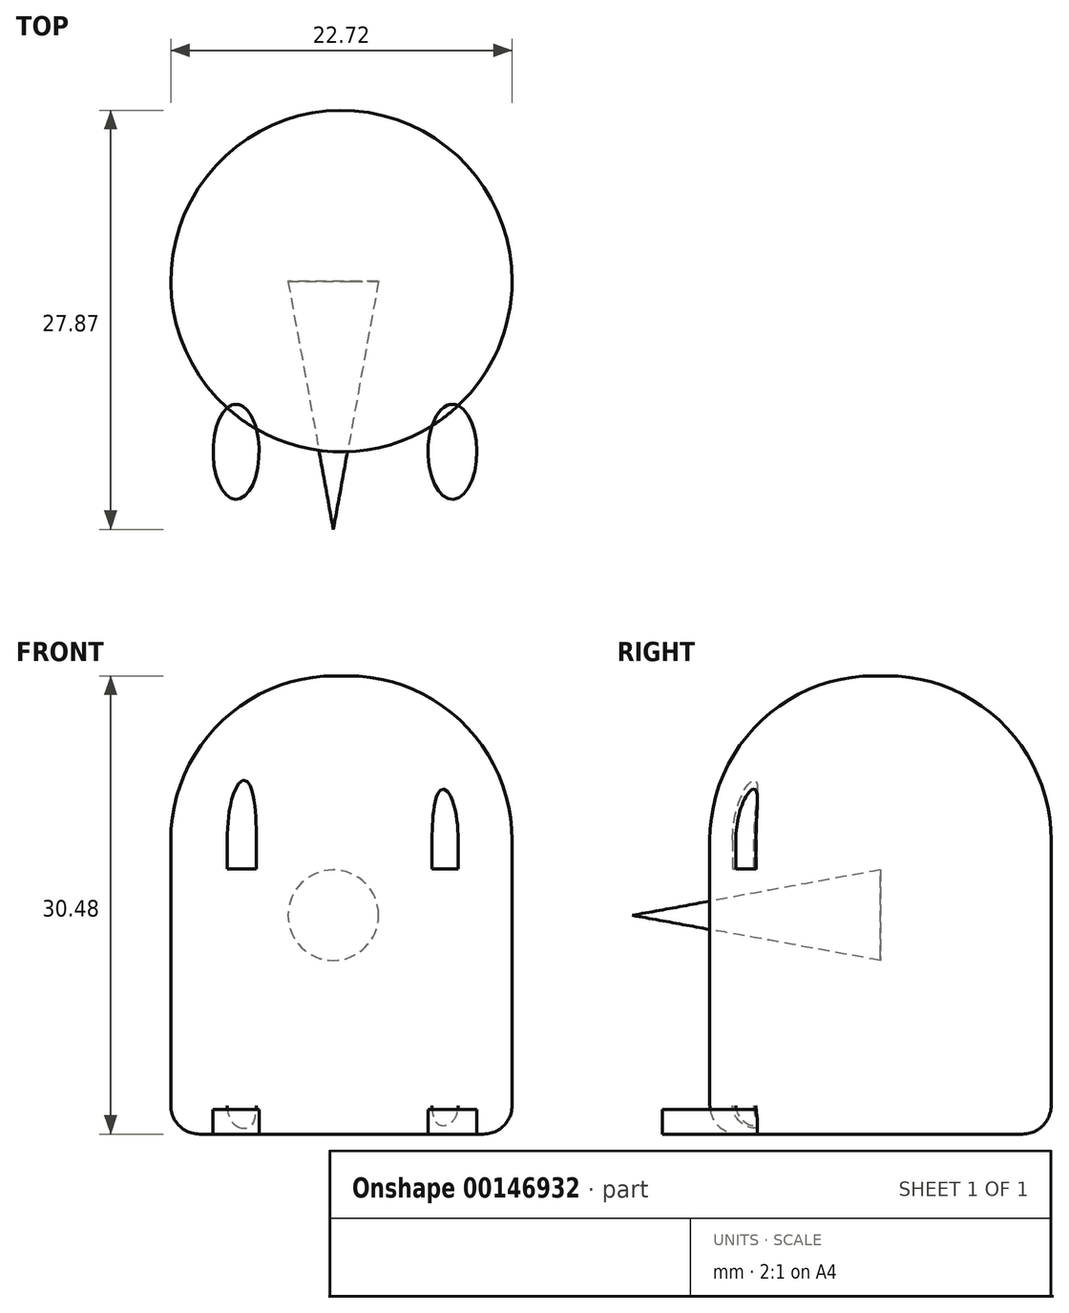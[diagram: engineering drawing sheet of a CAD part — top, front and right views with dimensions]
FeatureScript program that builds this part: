
annotation { "Feature Type Name" : "Feature", "Feature Type Description" : "" }
export const myFeature = defineFeature(function(context is Context, id is Id, definition is map)
    precondition{}
    {
        {
            var Q0;
            Q0=qCreatedBy(makeId("Top.planeOp"),FACE);
            var sketch = newSketch(context, id + "F0", { "sketchPlane" : qUnion([Q0])});
            skCircle(sketch, "E0", {"center": v(0, 0) * mm, "radius": 11.36 * mm});
            skPoint(sketch, "E1", {"position": v(0, -11.36) * mm});
            skEllipse(sketch, "E2", {"center": v(-7, -11.36) * mm, "majorRadius": 3.16 * mm, "minorRadius": 1.53 * mm, "majorAxis": v(0, 1)});
            skEllipse(sketch, "E3", {"center": v(7.39, -11.36) * mm, "majorRadius": 3.16 * mm, "minorRadius": 1.62 * mm, "majorAxis": v(0, 1)});
            skSolve(sketch);
        }
        {
            var Q0;
            {var subQ0=sQuery(id+"F0.wireOp",EDGE,"E2");var subQ1=sQuery(id+"F0.wireOp",EDGE,"E0");var subQ2=makeQuery(id+"F0.imprint","INTERSECT",VERTEX,{"disambiguationData":[OD(0.0)],"derivedFrom":[subQ1,subQ0]});Q0=makeQuery(id+"F0.imprint","IMPRINT",FACE,{"disambiguationData":[TD([[makeQuery(id+"F0.imprint","IMPRINT",EDGE,{"disambiguationData":[TD([[subQ2,-1.0]])],"derivedFrom":subQ1}),1.0]])]});}
            extrude(context, id + "F1", {"entities" : qUnion([Q0]), "depth" : 30.48 * mm});
        }
        {
            var Q0;
            Q0=makeQuery(id+"F1.opExtrude","CAP_EDGE",EDGE,{"disambiguationData":[OSD([sQuery(id+"F0.wireOp",EDGE,"E0")])],"isStart":false});
            fillet(context, id + "F2", {"entities" : qUnion([Q0]), "radius" : 10.92 * mm, "tangentPropagation" : true, "allowEdgeOverflow" : false});
        }
        {
            var Q0;
            Q0=makeQuery(id+"F1.opExtrude","CAP_EDGE",EDGE,{"disambiguationData":[OSD([sQuery(id+"F0.wireOp",EDGE,"E0")])],"isStart":true});
            fillet(context, id + "F3", {"entities" : qUnion([Q0]), "radius" : 1.9 * mm, "tangentPropagation" : true, "allowEdgeOverflow" : false});
        }
        {
            var Q0;
            {var subQ0=sQuery(id+"F0.wireOp",EDGE,"E3");var subQ1=sQuery(id+"F0.wireOp",EDGE,"E0");var subQ2=makeQuery(id+"F0.imprint","INTERSECT",VERTEX,{"disambiguationData":[OD(0.0)],"derivedFrom":[subQ1,subQ0]});Q0=makeQuery(id+"F0.imprint","IMPRINT",FACE,{"disambiguationData":[TD([[makeQuery(id+"F0.imprint","IMPRINT",EDGE,{"disambiguationData":[TD([[subQ2,-1.0]])],"derivedFrom":subQ1}),1.0]])]});}
            var Q1;
            {var subQ0=sQuery(id+"F0.wireOp",EDGE,"E2");var subQ1=sQuery(id+"F0.wireOp",EDGE,"E0");var subQ2=makeQuery(id+"F0.imprint","INTERSECT",VERTEX,{"disambiguationData":[OD(0.0)],"derivedFrom":[subQ1,subQ0]});Q1=makeQuery(id+"F0.imprint","IMPRINT",FACE,{"disambiguationData":[TD([[makeQuery(id+"F0.imprint","IMPRINT",EDGE,{"disambiguationData":[TD([[subQ2,1.0]])],"derivedFrom":subQ1}),1.0]])]});}
            extrude(context, id + "F4", {"entities" : qUnion([Q0, Q1]), "operationType" : NewBodyOperationType.ADD, "depth" : 17.65 * mm});
        }
        {
            var Q0;
            {var subQ0=sQuery(id+"F0.wireOp",EDGE,"E2");var subQ1=sQuery(id+"F0.wireOp",EDGE,"E0");var subQ2=makeQuery(id+"F0.imprint","INTERSECT",VERTEX,{"disambiguationData":[OD(0.0)],"derivedFrom":[subQ1,subQ0]});Q0=makeQuery(id+"F0.imprint","IMPRINT",FACE,{"disambiguationData":[TD([[makeQuery(id+"F0.imprint","IMPRINT",EDGE,{"disambiguationData":[TD([[subQ2,1.0]])],"derivedFrom":subQ1}),-1.0]])]});}
            var Q1;
            {var subQ0=sQuery(id+"F0.wireOp",EDGE,"E3");var subQ1=sQuery(id+"F0.wireOp",EDGE,"E0");var subQ2=makeQuery(id+"F0.imprint","INTERSECT",VERTEX,{"disambiguationData":[OD(0.0)],"derivedFrom":[subQ1,subQ0]});Q1=makeQuery(id+"F0.imprint","IMPRINT",FACE,{"disambiguationData":[TD([[makeQuery(id+"F0.imprint","IMPRINT",EDGE,{"disambiguationData":[TD([[subQ2,-1.0]])],"derivedFrom":subQ1}),-1.0]])]});}
            extrude(context, id + "F5", {"entities" : qUnion([Q0, Q1]), "operationType" : NewBodyOperationType.ADD, "depth" : 1.65 * mm});
        }
        {
            var Q0;
            Q0=qCreatedBy(makeId("Front.planeOp"),FACE);
            var sketch = newSketch(context, id + "F6", { "sketchPlane" : qUnion([Q0])});
            skPoint(sketch, "E4", {"position": v(-0.54, 14.56) * mm});
            skCircle(sketch, "E5", {"center": v(-0.54, 14.56) * mm, "radius": 3.01 * mm});
            skSolve(sketch);
        }
        {
            var Q0;
            Q0=qCreatedBy(makeId("Front.planeOp"),FACE);
            cPlane(context, id + "F7", {"entities" : qUnion([Q0]), "cplaneType" : CPlaneType.OFFSET, "offset" : 16.5 * mm, "width" : 152.4 * mm, "height" : 152.4 * mm});
        }
        {
            var Q0;
            Q0=qCreatedBy(id+"F7.planeOp",FACE);
            var sketch = newSketch(context, id + "F8", { "sketchPlane" : qUnion([Q0])});
            skPoint(sketch, "E6", {"position": v(-0.54, 14.55) * mm});
            skSolve(sketch);
        }
        {
            var Q0;
            Q0=makeQuery(id+"F6.imprint","IMPRINT",FACE,{"disambiguationData":[TD([[makeQuery(id+"F6.imprint","IMPRINT",EDGE,{"derivedFrom":sQuery(id+"F6.wireOp",EDGE,"E5")}),1.0]])]});
            var Q1;
            Q1=sQuery(id+"F8.wireOp",VERTEX,"E6");
            loft(context, id + "F9", {"sheetProfilesArray" : [{ "sheetProfileEntities" : qUnion([Q0]) }, { "sheetProfileEntities" : qUnion([Q1]) }]});
        }
    });
